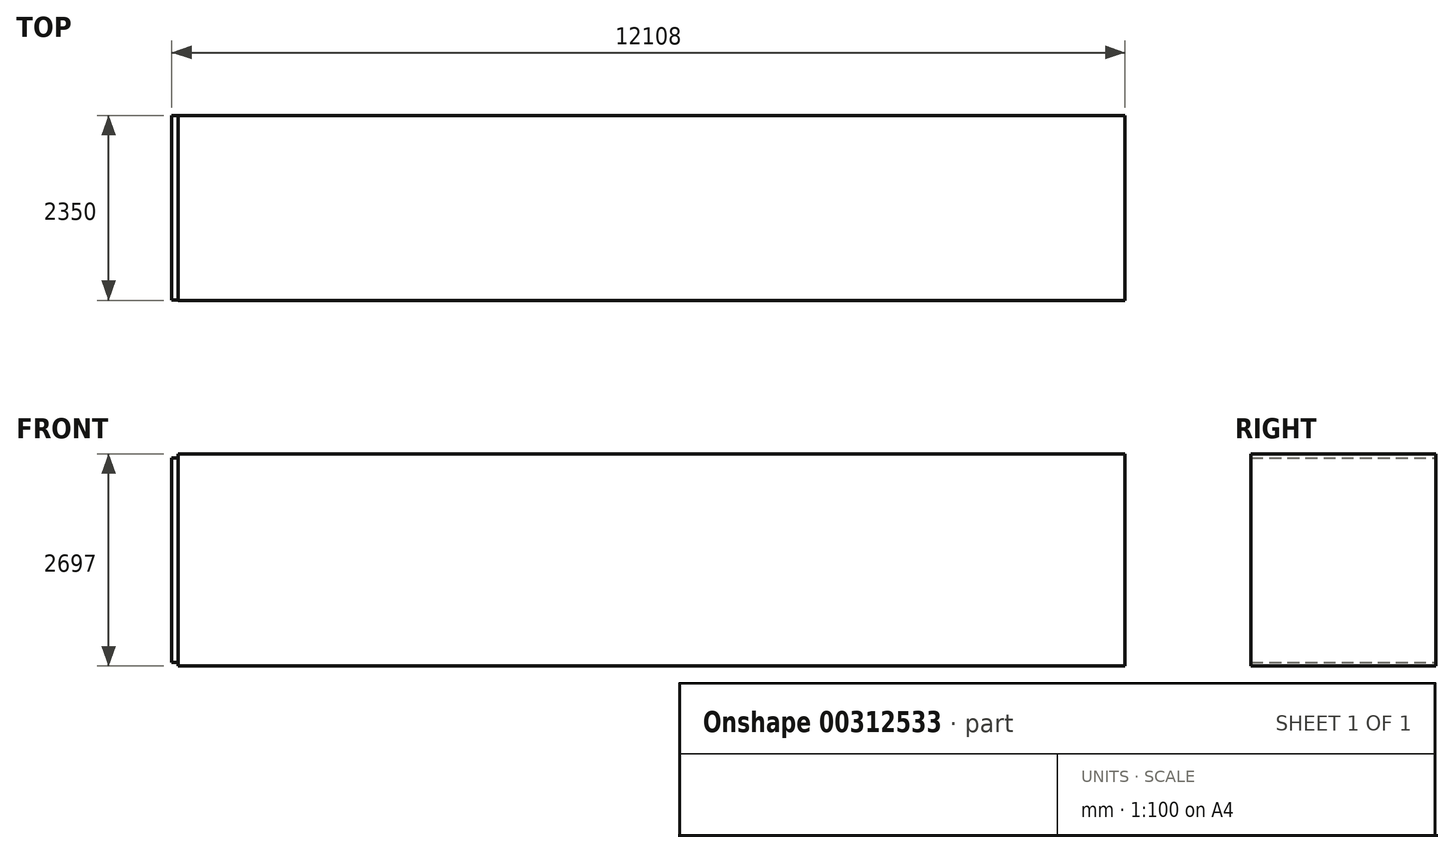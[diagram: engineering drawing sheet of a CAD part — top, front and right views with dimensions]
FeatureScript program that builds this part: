
annotation { "Feature Type Name" : "Feature", "Feature Type Description" : "" }
export const myFeature = defineFeature(function(context is Context, id is Id, definition is map)
    precondition{}
    {
        {
            var Q0;
            Q0=qCreatedBy(makeId("Top.planeOp"),FACE);
            var sketch = newSketch(context, id + "F0", { "sketchPlane" : qUnion([Q0])});
            skLineSegment(sketch, "E0.bottom", {"start": v(6012, -1175) * mm, "end": v(-6012, -1175) * mm});
            skLineSegment(sketch, "E0.top", {"start": v(6012, 1175) * mm, "end": v(-6012, 1175) * mm});
            skLineSegment(sketch, "E0.left", {"start": v(6012, -1175) * mm, "end": v(6012, 1175) * mm});
            skPoint(sketch, "E0.middle", {"position": v(0, 0) * mm});
            skLineSegment(sketch, "E1.bottom", {"start": v(6096, -1219) * mm, "end": v(-6096, -1219) * mm});
            skLineSegment(sketch, "E1.top", {"start": v(6096, 1219) * mm, "end": v(-6096, 1219) * mm});
            skLineSegment(sketch, "E1.left", {"start": v(6096, -1219) * mm, "end": v(6096, 1219) * mm});
            skLineSegment(sketch, "E1.right", {"start": v(-6096, -1219) * mm, "end": v(-6096, 1219) * mm});
            skLineSegment(sketch, "E2.bottom", {"start": v(-6012, -1170) * mm, "end": v(-6096, -1170) * mm});
            skLineSegment(sketch, "E2.top", {"start": v(-6012, 1170) * mm, "end": v(-6096, 1170) * mm});
            skPoint(sketch, "E2.middle", {"position": v(-6073.52, 0) * mm});
            skLineSegment(sketch, "E3", {"start": v(-6012, 1170) * mm, "end": v(-6012, 1175) * mm});
            skLineSegment(sketch, "E4", {"start": v(-6012, -1170) * mm, "end": v(-6012, -1175) * mm});
            skPoint(sketch, "E2.right.end.orphan", {"position": v(-6135.04, 1170) * mm});
            skPoint(sketch, "E5.orphan", {"position": v(-6135.04, -1170) * mm});
            skSolve(sketch);
        }
        {
            var Q0;
            Q0=makeQuery(id+"F0.imprint","IMPRINT",FACE,{"disambiguationData":[TD([[makeQuery(id+"F0.imprint","IMPRINT",EDGE,{"derivedFrom":sQuery(id+"F0.wireOp",EDGE,"E0.bottom")}),-1.0]])]});
            extrude(context, id + "F1", {"entities" : qUnion([Q0]), "depth" : 2697 * mm});
        }
        {
            var Q0;
            Q0=makeQuery(id+"F1.opExtrude","SWEPT_FACE",FACE,{"disambiguationData":[OSD([sQuery(id+"F0.wireOp",EDGE,"E1.right")])]});
            var sketch = newSketch(context, id + "F2", { "sketchPlane" : qUnion([Q0])});
            skLineSegment(sketch, "E6.bottom", {"start": v(1170, 50) * mm, "end": v(-1170, 50) * mm});
            skLineSegment(sketch, "E6.top", {"start": v(1170, 2647) * mm, "end": v(-1170, 2647) * mm});
            skLineSegment(sketch, "E6.left", {"start": v(1170, 50) * mm, "end": v(1170, 2647) * mm});
            skLineSegment(sketch, "E6.right", {"start": v(-1170, 50) * mm, "end": v(-1170, 2647) * mm});
            skPoint(sketch, "E6.middle", {"position": v(0, 1348.5) * mm});
            skPoint(sketch, "E6.middle.positionSnap0", {"position": v(1170, 1348.5) * mm});
            skPoint(sketch, "E6.centerSnap0", {"position": v(1170, 1348.5) * mm});
            skSolve(sketch);
        }
        {
            var Q0;
            {var subQ0=sQuery(id+"F2.wireOp",EDGE,"E6.top");Q0=makeQuery(id+"F2.imprint","IMPRINT",FACE,{"disambiguationData":[TD([[makeQuery(id+"F2.imprint","IMPRINT",EDGE,{"derivedFrom":subQ0}),-1.0]])]});}
            var Q1;
            {var subQ0=sQuery(id+"F2.wireOp",EDGE,"E6.bottom");Q1=makeQuery(id+"F2.imprint","IMPRINT",FACE,{"disambiguationData":[TD([[makeQuery(id+"F2.imprint","IMPRINT",EDGE,{"derivedFrom":subQ0}),1.0]])]});}
            var Q2;
            Q2=makeQuery(id+"F1.opExtrude","SWEPT_FACE",FACE,{"disambiguationData":[OSD([sQuery(id+"F0.wireOp",EDGE,"E4")])]});
            extrude(context, id + "F3", {"entities" : qUnion([Q0, Q1]), "operationType" : NewBodyOperationType.REMOVE, "endBound" : BoundingType.UP_TO_SURFACE, "oppositeDirection" : true, "endBoundEntityFace" : qUnion([Q2]), "depth" : 25 * mm});
        }
    });
